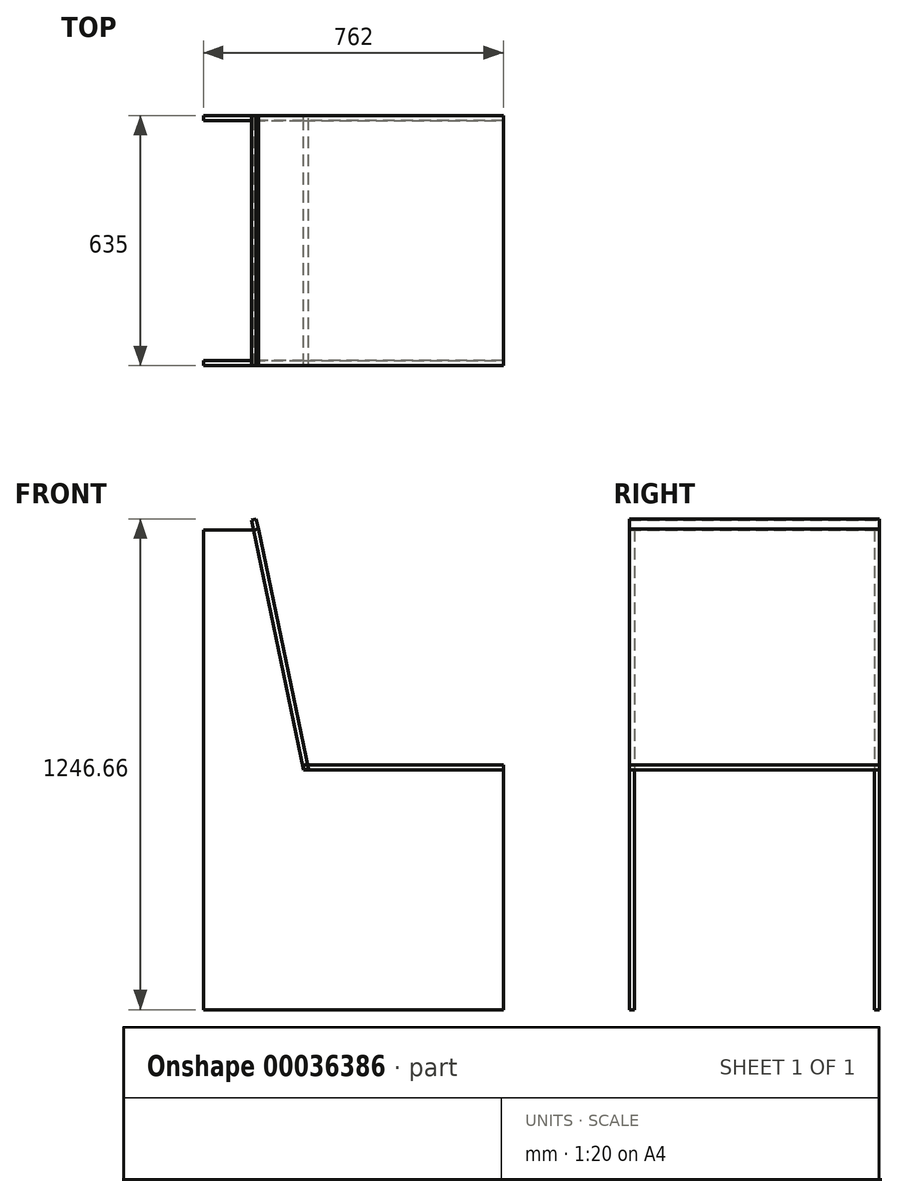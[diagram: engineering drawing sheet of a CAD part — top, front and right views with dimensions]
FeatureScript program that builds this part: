
annotation { "Feature Type Name" : "Feature", "Feature Type Description" : "" }
export const myFeature = defineFeature(function(context is Context, id is Id, definition is map)
    precondition{}
    {
        {
            var Q0;
            Q0=qCreatedBy(makeId("Front.planeOp"),FACE);
            var sketch = newSketch(context, id + "F0", { "sketchPlane" : qUnion([Q0])});
            skLineSegment(sketch, "E0", {"start": v(36.45, 609.6) * mm, "end": v(36.45, -609.6) * mm});
            skLineSegment(sketch, "E1", {"start": v(36.45, 609.6) * mm, "end": v(163.45, 609.6) * mm});
            skLineSegment(sketch, "E2", {"start": v(163.45, 609.6) * mm, "end": v(290.45, 0) * mm});
            skLineSegment(sketch, "E3", {"start": v(290.45, 0) * mm, "end": v(798.45, 0) * mm});
            skLineSegment(sketch, "E4", {"start": v(798.45, 0) * mm, "end": v(798.45, -609.6) * mm});
            skLineSegment(sketch, "E5", {"start": v(798.45, -609.6) * mm, "end": v(36.45, -609.6) * mm});
            skSolve(sketch);
        }
        {
            var Q0;
            Q0=makeQuery(id+"F0.imprint","IMPRINT",FACE,{"disambiguationData":[TD([[makeQuery(id+"F0.imprint","IMPRINT",EDGE,{"derivedFrom":sQuery(id+"F0.wireOp",EDGE,"E0")}),1.0]])]});
            extrude(context, id + "F1", {"entities" : qUnion([Q0]), "depth" : 12.7 * mm});
        }
        {
            var Q0;
            Q0=makeQuery(id+"F1.opExtrude","CAP_FACE",FACE,{"disambiguationData":[OSD([sQuery(id+"F0.wireOp",EDGE,"E0"),sQuery(id+"F0.wireOp",EDGE,"E1"),sQuery(id+"F0.wireOp",EDGE,"E2"),sQuery(id+"F0.wireOp",EDGE,"E3"),sQuery(id+"F0.wireOp",EDGE,"E4"),sQuery(id+"F0.wireOp",EDGE,"E5")])],"isStart":false});
            cPlane(context, id + "F2", {"entities" : qUnion([Q0]), "cplaneType" : CPlaneType.OFFSET, "offset" : 609.6 * mm, "width" : 152.4 * mm, "height" : 152.4 * mm});
        }
        {
            var Q0;
            Q0=qCreatedBy(id+"F2.planeOp",FACE);
            var sketch = newSketch(context, id + "F3", { "sketchPlane" : qUnion([Q0])});
            skLineSegment(sketch, "E6.0", {"start": v(36.45, 609.6) * mm, "end": v(163.45, 609.6) * mm});
            skLineSegment(sketch, "E7.0", {"start": v(163.45, 609.6) * mm, "end": v(290.45, 0) * mm});
            skLineSegment(sketch, "E8.0", {"start": v(36.45, 609.6) * mm, "end": v(36.45, -609.6) * mm});
            skLineSegment(sketch, "E9.0", {"start": v(798.45, -609.6) * mm, "end": v(36.45, -609.6) * mm});
            skLineSegment(sketch, "E10.0", {"start": v(798.45, 0) * mm, "end": v(798.45, -609.6) * mm});
            skLineSegment(sketch, "E11.0", {"start": v(290.45, 0) * mm, "end": v(798.45, 0) * mm});
            skSolve(sketch);
        }
        {
            var Q0;
            Q0=makeQuery(id+"F3.imprint","IMPRINT",FACE,{"disambiguationData":[TD([[makeQuery(id+"F3.imprint","IMPRINT",EDGE,{"derivedFrom":sQuery(id+"F3.wireOp",EDGE,"E6.0")}),-1.0]])]});
            extrude(context, id + "F4", {"entities" : qUnion([Q0]), "depth" : 12.7 * mm});
        }
        {
            var Q0;
            Q0=makeQuery(id+"F4.opExtrude","SWEPT_FACE",FACE,{"disambiguationData":[OSD([sQuery(id+"F3.wireOp",EDGE,"E11.0")])]});
            var sketch = newSketch(context, id + "F5", { "sketchPlane" : qUnion([Q0])});
            skLineSegment(sketch, "E12.0", {"start": v(290.45, 0) * mm, "end": v(798.45, 0) * mm});
            skLineSegment(sketch, "E13.0", {"start": v(290.45, -635) * mm, "end": v(798.45, -635) * mm});
            skLineSegment(sketch, "E14.left", {"start": v(290.45, 0) * mm, "end": v(290.45, -635) * mm});
            skLineSegment(sketch, "E14.right", {"start": v(798.45, 0) * mm, "end": v(798.45, -635) * mm});
            skSolve(sketch);
        }
        {
            var Q0;
            {var subQ2=sQuery(id+"F5.wireOp",EDGE,"E12.0");Q0=makeQuery(id+"F5.imprint","IMPRINT",FACE,{"disambiguationData":[TD([[makeQuery(id+"F5.imprint","IMPRINT",EDGE,{"derivedFrom":subQ2}),-1.0]])]});}
            var Q1;
            {var subQ2=sQuery(id+"F5.wireOp",EDGE,"E13.0");Q1=makeQuery(id+"F5.imprint","IMPRINT",FACE,{"disambiguationData":[TD([[makeQuery(id+"F5.imprint","IMPRINT",EDGE,{"derivedFrom":subQ2}),1.0]])]});}
            extrude(context, id + "F6", {"entities" : qUnion([Q0, Q1]), "depth" : 12.7 * mm});
        }
        {
            var Q0;
            Q0=makeQuery(id+"F4.opExtrude","SWEPT_FACE",FACE,{"disambiguationData":[OSD([sQuery(id+"F3.wireOp",EDGE,"E7.0")])]});
            var sketch = newSketch(context, id + "F7", { "sketchPlane" : qUnion([Q0])});
            skLineSegment(sketch, "E15.0", {"start": v(-635, 563.45) * mm, "end": v(-635, -59.24) * mm});
            skLineSegment(sketch, "E16.0", {"start": v(0, 563.45) * mm, "end": v(0, -59.24) * mm});
            skLineSegment(sketch, "E17.bottom", {"start": v(-635, 563.45) * mm, "end": v(0, 563.45) * mm});
            skLineSegment(sketch, "E17.top", {"start": v(-635, -59.24) * mm, "end": v(0, -59.24) * mm});
            skSolve(sketch);
        }
        {
            var Q0;
            {var subQ1=sQuery(id+"F7.wireOp",EDGE,"E16.0");Q0=makeQuery(id+"F7.imprint","IMPRINT",FACE,{"disambiguationData":[TD([[makeQuery(id+"F7.imprint","IMPRINT",EDGE,{"derivedFrom":subQ1}),-1.0]])]});}
            var Q1;
            {var subQ1=sQuery(id+"F7.wireOp",EDGE,"E15.0");Q1=makeQuery(id+"F7.imprint","IMPRINT",FACE,{"disambiguationData":[TD([[makeQuery(id+"F7.imprint","IMPRINT",EDGE,{"derivedFrom":subQ1}),1.0]])]});}
            extrude(context, id + "F8", {"entities" : qUnion([Q0, Q1]), "depth" : 12.7 * mm});
        }
        {
            var Q0;
            Q0=makeQuery(id+"F1.opExtrude","SWEPT_FACE",FACE,{"disambiguationData":[OSD([sQuery(id+"F0.wireOp",EDGE,"E1")])]});
            var sketch = newSketch(context, id + "F9", { "sketchPlane" : qUnion([Q0])});
            skLineSegment(sketch, "E18.0", {"start": v(36.45, 0) * mm, "end": v(163.45, 0) * mm});
            skLineSegment(sketch, "E19.0", {"start": v(36.45, -635) * mm, "end": v(163.45, -635) * mm});
            skLineSegment(sketch, "E20.left", {"start": v(36.45, 0) * mm, "end": v(36.45, -635) * mm});
            skLineSegment(sketch, "E20.right", {"start": v(163.45, 0) * mm, "end": v(163.45, -635) * mm});
            skSolve(sketch);
        }
        {
            var Q0;
            {var subQ2=sQuery(id+"F9.wireOp",EDGE,"E18.0");Q0=makeQuery(id+"F9.imprint","IMPRINT",FACE,{"disambiguationData":[TD([[makeQuery(id+"F9.imprint","IMPRINT",EDGE,{"derivedFrom":subQ2}),-1.0]])]});}
            var Q1;
            Q1=makeQuery(id+"F8.opExtrude","SWEPT_FACE",FACE,{"disambiguationData":[OSD([sQuery(id+"F7.wireOp",EDGE,"E17.bottom")])]});
            var Q2;
            {var subQ2=sQuery(id+"F9.wireOp",EDGE,"E19.0");Q2=makeQuery(id+"F9.imprint","IMPRINT",FACE,{"disambiguationData":[TD([[makeQuery(id+"F9.imprint","IMPRINT",EDGE,{"derivedFrom":subQ2}),1.0]])]});}
            extrude(context, id + "F10", {"entities" : qUnion([Q0, Q1, Q2]), "depth" : 25.4 * mm});
        }
    });
